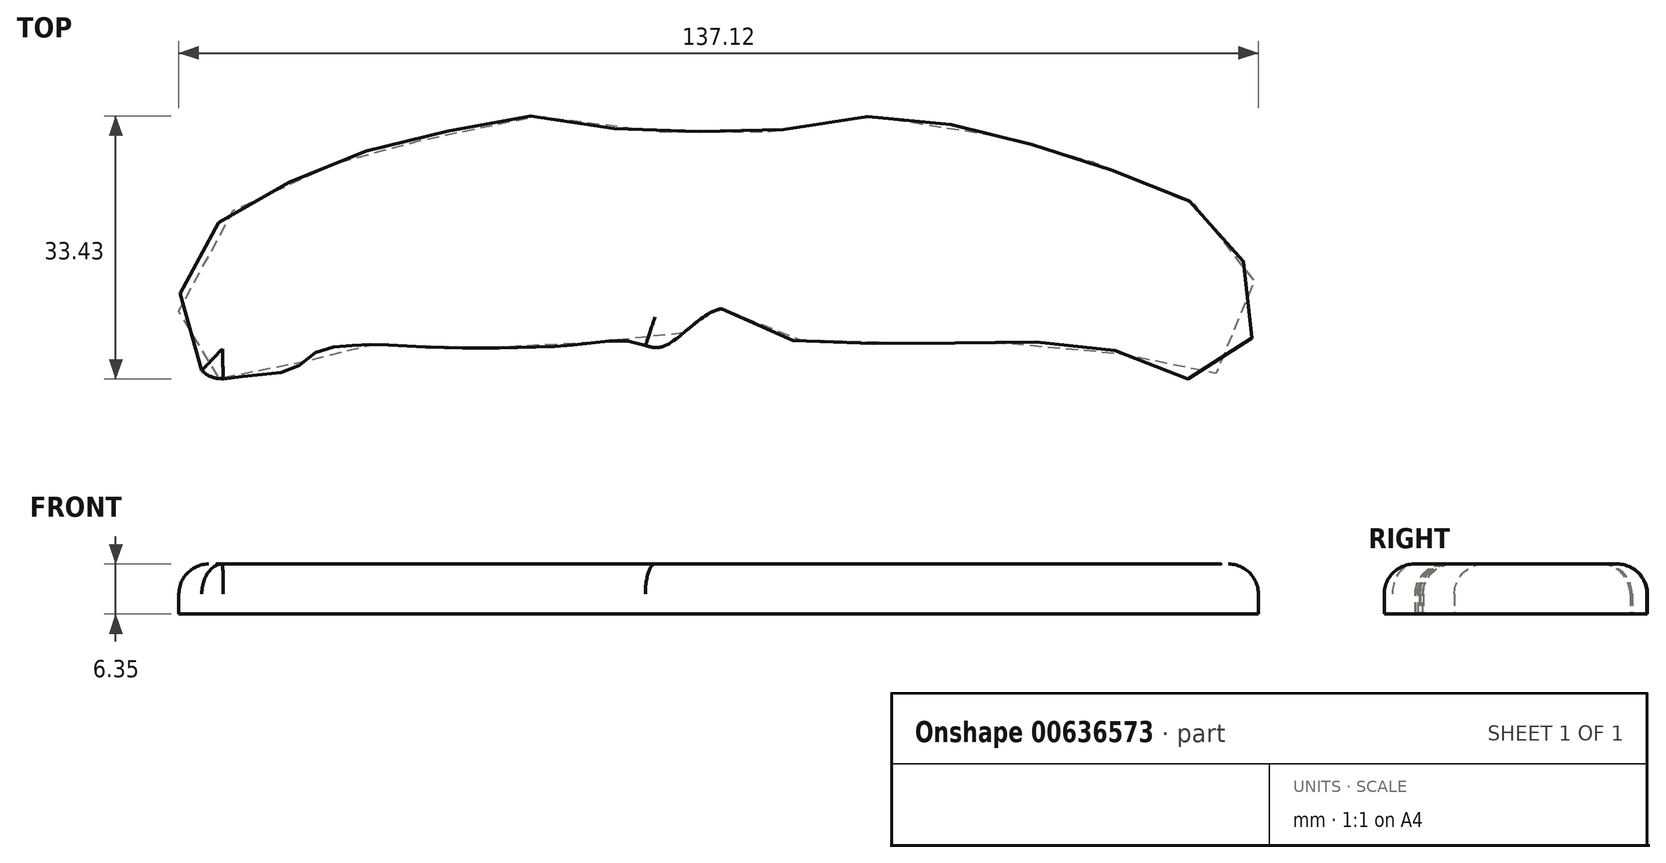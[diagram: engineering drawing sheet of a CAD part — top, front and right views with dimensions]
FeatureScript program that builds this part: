
annotation { "Feature Type Name" : "Feature", "Feature Type Description" : "" }
export const myFeature = defineFeature(function(context is Context, id is Id, definition is map)
    precondition{}
    {
        {
            var Q0;
            Q0=qCreatedBy(makeId("Top.planeOp"),FACE);
            var sketch = newSketch(context, id + "F0", { "sketchPlane" : qUnion([Q0])});
            skFitSpline(sketch, "E0", {"points": [v(-0.66, -0.85) * mm, v(-8.06, -5.6) * mm, v(-12.04, -5.02) * mm, v(-19.24, -5.4) * mm, v(-27.4, -5.78) * mm, v(-35.74, -5.78) * mm, v(-44.65, -5.4) * mm, v(-48.82, -5.6) * mm, v(-52.23, -6.35) * mm, v(-55.08, -8.44) * mm, v(-60.96, -9.39) * mm, v(-65.32, -9.57) * mm, v(-67.97, -7.1) * mm, v(-69.68, -1.42) * mm, v(-67.21, 7.1) * mm, v(-59.63, 13.56) * mm, v(-51.67, 16.78) * mm, v(-46.36, 19.05) * mm, v(-41.62, 19.81) * mm, v(-33.08, 22.47) * mm, v(-23.98, 23.6) * mm, v(-13.37, 21.9) * mm, v(-4.27, 21.7) * mm, v(3.5, 21.52) * mm, v(11.85, 22.85) * mm, v(19.24, 23.6) * mm, v(30.62, 22.09) * mm, v(39.53, 19.81) * mm, v(44.27, 18.68) * mm, v(51.48, 15.64) * mm, v(59.06, 12.6) * mm, v(62.66, 8.63) * mm, v(67.02, 2.37) * mm, v(65.89, -5.97) * mm, v(60.2, -9.57) * mm, v(53, -8.63) * mm, v(47.11, -5.21) * mm, v(37.45, -5.21) * mm, v(30.24, -5.21) * mm, v(21.7, -5.21) * mm, v(15.45, -5.21) * mm, v(8.25, -4.83) * mm, v(4.46, -4.08) * mm, v(-0.66, -0.85) * mm]});
            skSolve(sketch);
        }
        {
            var Q0;
            Q0 = qSketchRegion(id + "F0", true);
            extrude(context, id + "F1", {"entities" : qUnion([Q0]), "depth" : 6.35 * mm, "offsetDistance" : 25.4 * mm});
        }
        {
            var Q0;
            Q0=makeQuery(id+"F1.opExtrude","CAP_EDGE",EDGE,{"disambiguationData":[OSD([sQuery(id+"F0.wireOp",EDGE,"E0")])],"isStart":false});
            fillet(context, id + "F2", {"entities" : qUnion([Q0]), "radius" : 3.8 * mm, "tangentPropagation" : true, "allowEdgeOverflow" : false});
        }
    });
